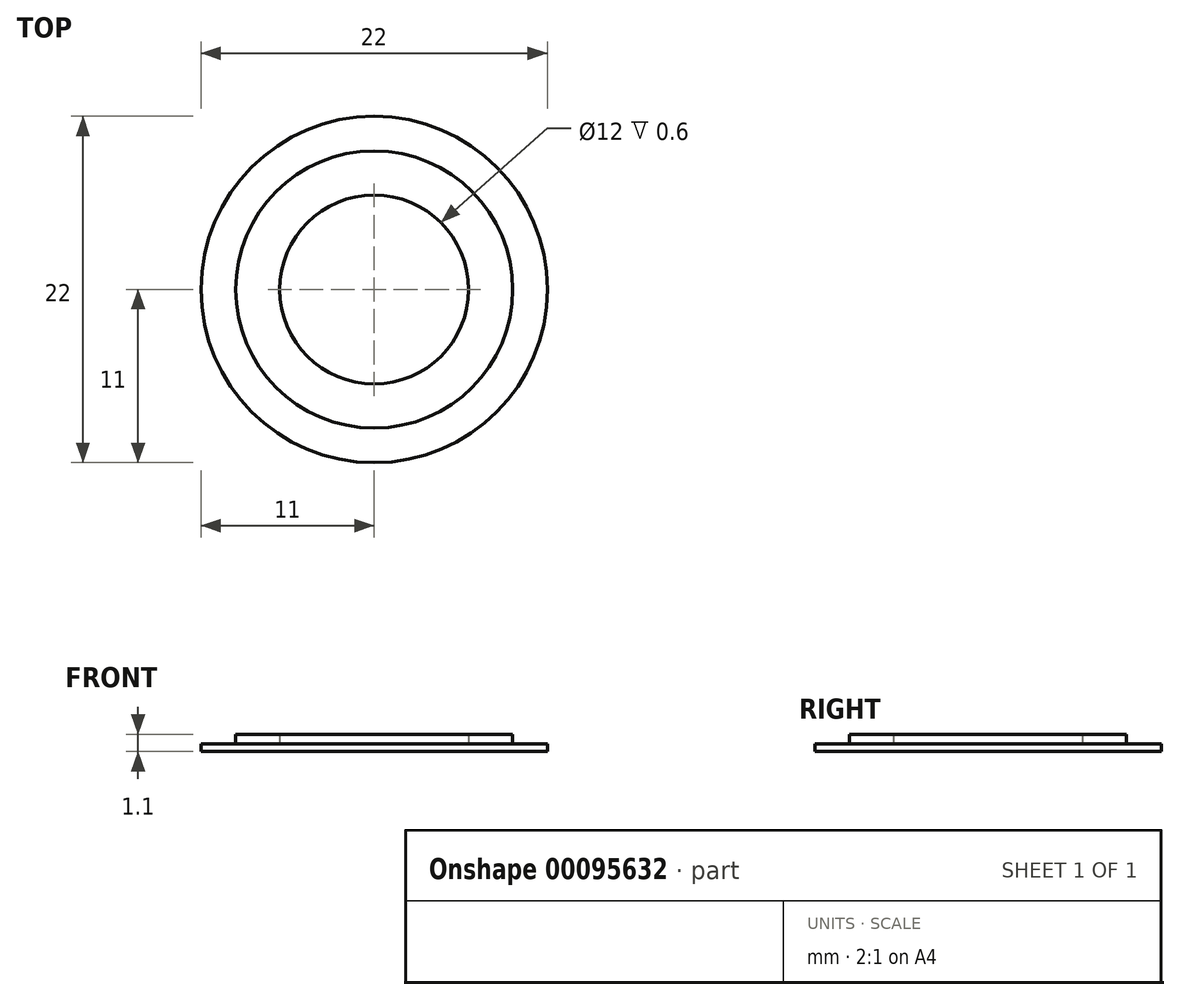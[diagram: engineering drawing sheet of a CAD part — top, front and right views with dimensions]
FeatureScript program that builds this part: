
annotation { "Feature Type Name" : "Feature", "Feature Type Description" : "" }
export const myFeature = defineFeature(function(context is Context, id is Id, definition is map)
    precondition{}
    {
        {
            var Q0;
            Q0=qCreatedBy(makeId("Top.planeOp"),FACE);
            var sketch = newSketch(context, id + "F0", { "sketchPlane" : qUnion([Q0])});
            skCircle(sketch, "E0", {"center": v(0, 0) * mm, "radius": 8.8 * mm});
            skCircle(sketch, "E1", {"center": v(0, 0) * mm, "radius": 6 * mm});
            skSolve(sketch);
        }
        {
            var Q0;
            Q0=qSketchRegion(id+"F0",true);
            extrude(context, id + "F1", {"entities" : qUnion([Q0]), "depth" : .6 * mm});
        }
        {
            var Q0;
            Q0=qCreatedBy(makeId("Top.planeOp"),FACE);
            var sketch = newSketch(context, id + "F2", { "sketchPlane" : qUnion([Q0])});
            skCircle(sketch, "E2", {"center": v(0, 0) * mm, "radius": 11 * mm});
            skSolve(sketch);
        }
        {
            var Q0;
            Q0=qSketchRegion(id+"F2",true);
            extrude(context, id + "F3", {"entities" : qUnion([Q0]), "oppositeDirection" : true, "depth" : .5 * mm});
        }
    });
